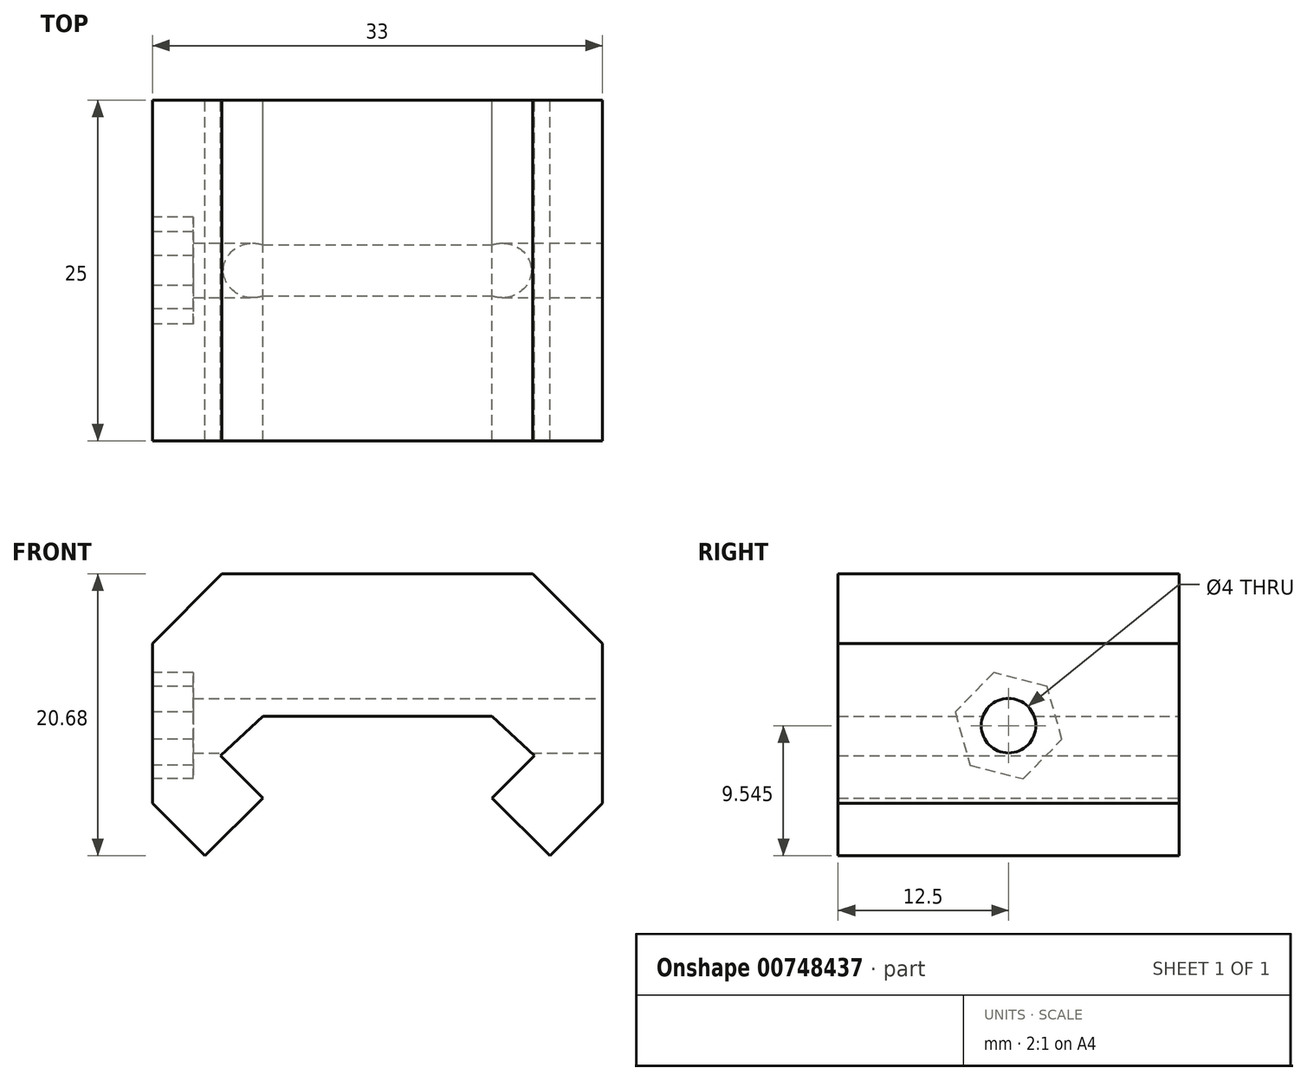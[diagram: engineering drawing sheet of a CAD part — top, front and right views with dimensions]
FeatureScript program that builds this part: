
annotation { "Feature Type Name" : "Feature", "Feature Type Description" : "" }
export const myFeature = defineFeature(function(context is Context, id is Id, definition is map)
    precondition{}
    {
        {
            var Q0;
            Q0=qCreatedBy(makeId("Front.planeOp"),FACE);
            var sketch = newSketch(context, id + "F0", { "sketchPlane" : qUnion([Q0])});
            skLineSegment(sketch, "E0", {"start": v(-8.3, 0) * mm, "end": v(8.5, 0) * mm});
            skLineSegment(sketch, "E1", {"start": v(-8.3, 0) * mm, "end": v(-11.4, -2.9) * mm});
            skLineSegment(sketch, "E2", {"start": v(-11.4, -2.9) * mm, "end": v(-8.3, -6) * mm});
            skLineSegment(sketch, "E3", {"start": v(-8.3, -6) * mm, "end": v(-12.54, -10.24) * mm});
            skLineSegment(sketch, "E4", {"start": v(-12.54, -10.24) * mm, "end": v(-22.26, -0.52) * mm});
            skLineSegment(sketch, "E5", {"start": v(-22.26, -0.52) * mm, "end": v(-11.3, 10.44) * mm});
            skLineSegment(sketch, "E6", {"start": v(-11.3, 10.44) * mm, "end": v(11.5, 10.44) * mm});
            skLineSegment(sketch, "E7", {"start": v(11.5, 10.44) * mm, "end": v(22.46, -0.52) * mm});
            skLineSegment(sketch, "E8", {"start": v(22.46, -0.52) * mm, "end": v(12.74, -10.24) * mm});
            skLineSegment(sketch, "E9", {"start": v(12.74, -10.24) * mm, "end": v(8.5, -6) * mm});
            skLineSegment(sketch, "E10", {"start": v(8.5, -6) * mm, "end": v(11.6, -2.9) * mm});
            skLineSegment(sketch, "E11", {"start": v(11.6, -2.9) * mm, "end": v(8.5, 0) * mm});
            skSolve(sketch);
        }
        {
            var Q0;
            Q0=qSketchRegion(id+"F0",true);
            extrude(context, id + "F1", {"entities" : qUnion([Q0]), "depth" : 25 * mm, "offsetDistance" : 25 * mm});
        }
        {
            var Q0;
            Q0=makeQuery(id+"F1.opExtrude","CAP_FACE",FACE,{"disambiguationData":[OSD([sQuery(id+"F0.wireOp",EDGE,"E0"),sQuery(id+"F0.wireOp",EDGE,"E1"),sQuery(id+"F0.wireOp",EDGE,"E2"),sQuery(id+"F0.wireOp",EDGE,"E3"),sQuery(id+"F0.wireOp",EDGE,"E4"),sQuery(id+"F0.wireOp",EDGE,"E5"),sQuery(id+"F0.wireOp",EDGE,"E6"),sQuery(id+"F0.wireOp",EDGE,"E7"),sQuery(id+"F0.wireOp",EDGE,"E8"),sQuery(id+"F0.wireOp",EDGE,"E9"),sQuery(id+"F0.wireOp",EDGE,"E10"),sQuery(id+"F0.wireOp",EDGE,"E11")])],"isStart":false});
            var sketch = newSketch(context, id + "F2", { "sketchPlane" : qUnion([Q0])});
            skLineSegment(sketch, "E12.bottom", {"start": v(-24, 10) * mm, "end": v(-16.4, 10) * mm});
            skLineSegment(sketch, "E12.top", {"start": v(-24, -11.1) * mm, "end": v(-16.4, -11.1) * mm});
            skLineSegment(sketch, "E12.left", {"start": v(-24, 10) * mm, "end": v(-24, -11.1) * mm});
            skLineSegment(sketch, "E12.right", {"start": v(-16.4, 10) * mm, "end": v(-16.4, -11.1) * mm});
            skLineSegment(sketch, "E13.bottom", {"start": v(26.87, 13.5) * mm, "end": v(16.6, 13.5) * mm});
            skLineSegment(sketch, "E13.top", {"start": v(26.87, -16.6) * mm, "end": v(16.6, -16.6) * mm});
            skLineSegment(sketch, "E13.left", {"start": v(26.87, 13.5) * mm, "end": v(26.87, -16.6) * mm});
            skLineSegment(sketch, "E13.right", {"start": v(16.6, 13.5) * mm, "end": v(16.6, -16.6) * mm});
            skSolve(sketch);
        }
        {
            var Q0;
            Q0=qSketchRegion(id+"F2",true);
            extrude(context, id + "F3", {"entities" : qUnion([Q0]), "operationType" : NewBodyOperationType.REMOVE, "oppositeDirection" : true, "depth" : 25 * mm, "offsetDistance" : 25 * mm});
        }
        {
            var Q0;
            Q0=makeQuery(id+"F3.boolean.opBoolean","COPY",FACE,{"derivedFrom":makeQuery(id+"F3.opExtrude","SWEPT_FACE",FACE,{"disambiguationData":[OSD([sQuery(id+"F2.wireOp",EDGE,"E13.right")])]})});
            var sketch = newSketch(context, id + "F4", { "sketchPlane" : qUnion([Q0])});
            skCircle(sketch, "E14", {"center": v(-12.5, -0.7) * mm, "radius": 2 * mm});
            skSolve(sketch);
        }
        {
            var Q0;
            Q0=qSketchRegion(id+"F4",true);
            extrude(context, id + "F5", {"entities" : qUnion([Q0]), "operationType" : NewBodyOperationType.REMOVE, "oppositeDirection" : true, "depth" : 35 * mm, "offsetDistance" : 25 * mm});
        }
        {
            var Q0;
            Q0=makeQuery(id+"F3.boolean.opBoolean","COPY",FACE,{"derivedFrom":makeQuery(id+"F3.opExtrude","SWEPT_FACE",FACE,{"disambiguationData":[OSD([sQuery(id+"F2.wireOp",EDGE,"E12.right")])]})});
            var sketch = newSketch(context, id + "F6", { "sketchPlane" : qUnion([Q0])});
            skCircle(sketch, "E15.cCircle", {"center": v(12.5, -0.7) * mm, "radius": 3.5 * mm, "construction": true});
            skLineSegment(sketch, "E15.0", {"start": v(16.42, 0.3) * mm, "end": v(15.32, -3.59) * mm});
            skLineSegment(sketch, "E15.1", {"start": v(15.32, -3.59) * mm, "end": v(11.4, -4.59) * mm});
            skLineSegment(sketch, "E15.2", {"start": v(11.4, -4.59) * mm, "end": v(8.58, -1.7) * mm});
            skLineSegment(sketch, "E15.3", {"start": v(8.58, -1.7) * mm, "end": v(9.68, 2.2) * mm});
            skLineSegment(sketch, "E15.4", {"start": v(9.68, 2.2) * mm, "end": v(13.6, 3.2) * mm});
            skLineSegment(sketch, "E15.5", {"start": v(13.6, 3.2) * mm, "end": v(16.42, 0.3) * mm});
            skPoint(sketch, "E15.0.midPoint", {"position": v(15.87, -1.64) * mm});
            skSolve(sketch);
        }
        {
            var Q0;
            Q0=qSketchRegion(id+"F6",true);
            extrude(context, id + "F7", {"entities" : qUnion([Q0]), "operationType" : NewBodyOperationType.REMOVE, "oppositeDirection" : true, "depth" : 3 * mm, "offsetDistance" : 25 * mm});
        }
    });
